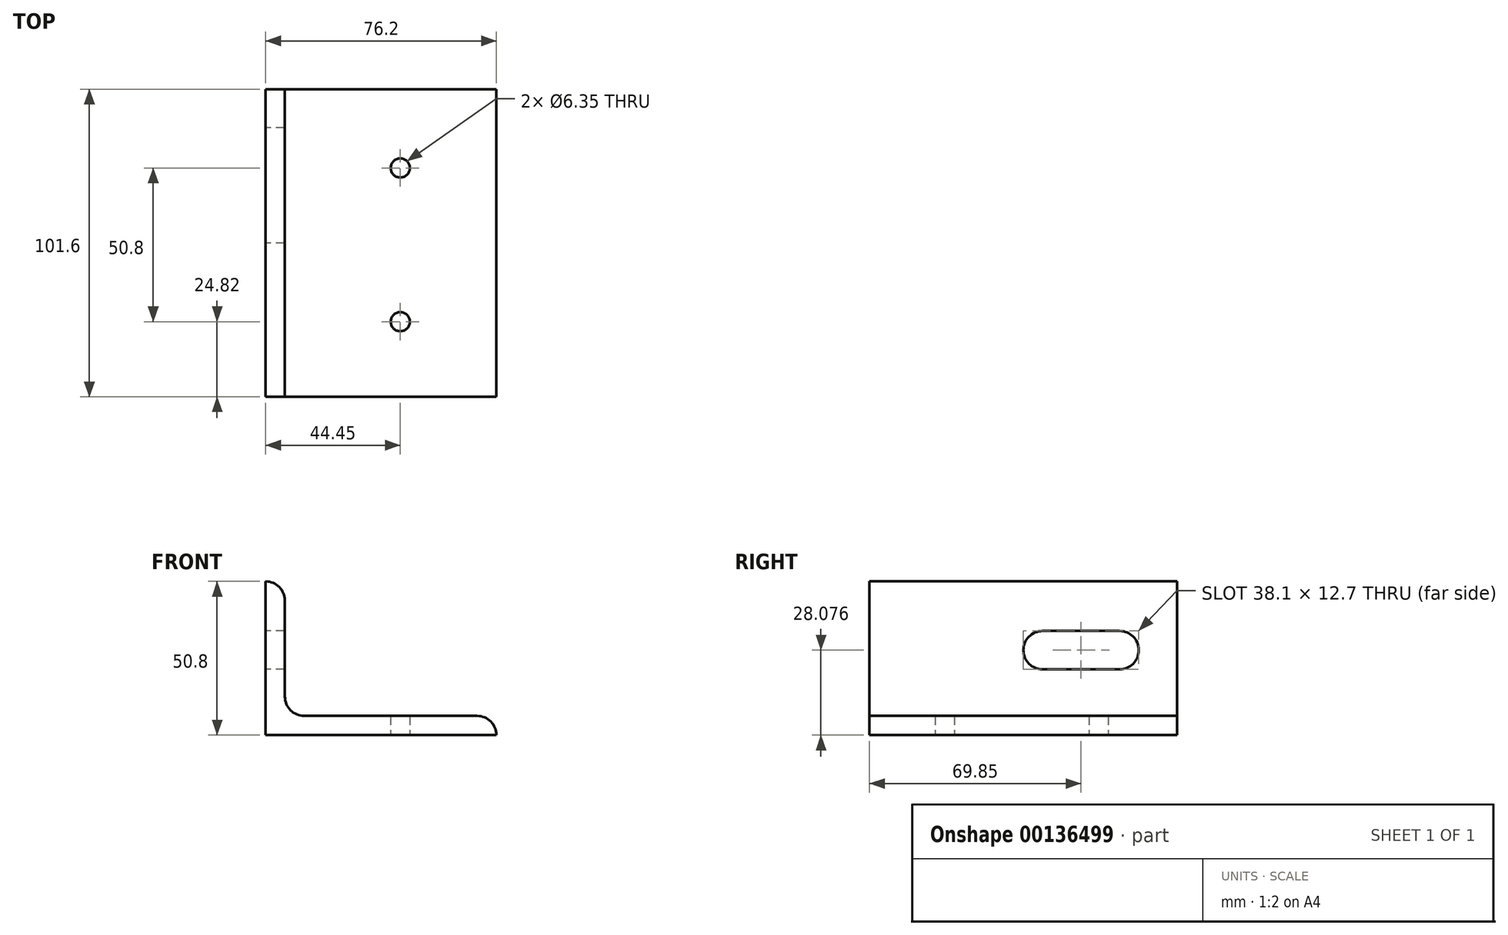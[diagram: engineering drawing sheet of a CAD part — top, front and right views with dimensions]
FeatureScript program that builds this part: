
annotation { "Feature Type Name" : "Feature", "Feature Type Description" : "" }
export const myFeature = defineFeature(function(context is Context, id is Id, definition is map)
    precondition{}
    {
        {
            var Q0;
            Q0=qCreatedBy(makeId("Front.planeOp"),FACE);
            var sketch = newSketch(context, id + "F0", { "sketchPlane" : qUnion([Q0])});
            skLineSegment(sketch, "E0", {"start": v(0, 50.8) * mm, "end": v(0, 0) * mm});
            skLineSegment(sketch, "E1", {"start": v(0, 0) * mm, "end": v(76.2, 0) * mm});
            skArc(sketch, "E2", {"start": v(6.35, 44.45) * mm, "mid": v(4.5, 48.94) * mm, "end": v(0, 50.8) * mm});
            skLineSegment(sketch, "E3", {"start": v(6.35, 44.45) * mm, "end": v(6.35, 6.35) * mm});
            skLineSegment(sketch, "E4", {"start": v(6.35, 6.35) * mm, "end": v(69.85, 6.35) * mm});
            skArc(sketch, "E5", {"start": v(76.2, 0) * mm, "mid": v(74.34, 4.5) * mm, "end": v(69.85, 6.35) * mm});
            skSolve(sketch);
        }
        {
            var Q0;
            Q0=makeQuery(id+"F0.imprint","IMPRINT",FACE,{"disambiguationData":[TD([[makeQuery(id+"F0.imprint","IMPRINT",EDGE,{"derivedFrom":sQuery(id+"F0.wireOp",EDGE,"E0")}),1.0]])]});
            extrude(context, id + "F1", {"entities" : qUnion([Q0]), "endBound" : BoundingType.SYMMETRIC, "depth" : 101.6 * mm});
        }
        {
            var Q0;
            Q0=makeQuery(id+"F1.opExtrude","SWEPT_EDGE",EDGE,{"disambiguationData":[OSD([sQuery(id+"F0.wireOp",EDGE,"E3"),sQuery(id+"F0.wireOp",EDGE,"E4")])]});
            fillet(context, id + "F2", {"entities" : qUnion([Q0]), "radius" : 6.35 * mm, "tangentPropagation" : true, "allowEdgeOverflow" : false});
        }
        {
            var Q0;
            Q0=makeQuery(id+"F1.opExtrude","SWEPT_FACE",FACE,{"disambiguationData":[OSD([sQuery(id+"F0.wireOp",EDGE,"E1")])]});
            var sketch = newSketch(context, id + "F3", { "sketchPlane" : qUnion([Q0])});
            skPoint(sketch, "E6", {"position": v(44.45, 25.98) * mm});
            skPoint(sketch, "E7", {"position": v(44.45, -24.82) * mm});
            skSolve(sketch);
        }
        {
            var Q0;
            Q0=sQuery(id+"F3.wireOp",VERTEX,"E6");
            var Q1;
            Q1=sQuery(id+"F3.wireOp",VERTEX,"E7");
            var Q2;
            Q2=makeQuery(id+"F1.opExtrude","SWEPT_BODY",BODY,{"disambiguationData":[OSD([sQuery(id+"F0.wireOp",EDGE,"E0"),sQuery(id+"F0.wireOp",EDGE,"E1"),sQuery(id+"F0.wireOp",EDGE,"E2"),sQuery(id+"F0.wireOp",EDGE,"E3"),sQuery(id+"F0.wireOp",EDGE,"E4"),sQuery(id+"F0.wireOp",EDGE,"E5")])]});
            hole(context, id + "F4", {"style" : HoleStyle.SIMPLE, "endStyle" : HoleEndStyle.THROUGH, "holeDiameter" : 6.35 * mm, "locations" : qUnion([Q0, Q1]), "scope" : qUnion([Q2]), "isTappedThrough" : true});
        }
        {
            var Q0;
            Q0=makeQuery(id+"F1.opExtrude","SWEPT_FACE",FACE,{"disambiguationData":[OSD([sQuery(id+"F0.wireOp",EDGE,"E0")])]});
            var sketch = newSketch(context, id + "F5", { "sketchPlane" : qUnion([Q0])});
            skArc(sketch, "E8", {"start": v(-31.75, 34.43) * mm, "mid": v(-38.1, 28.08) * mm, "end": v(-31.75, 21.73) * mm});
            skArc(sketch, "E9", {"start": v(-6.35, 21.73) * mm, "mid": v(0, 28.08) * mm, "end": v(-6.35, 34.43) * mm});
            skLineSegment(sketch, "E10", {"start": v(-31.75, 34.43) * mm, "end": v(-6.35, 34.43) * mm});
            skLineSegment(sketch, "E11", {"start": v(-31.75, 21.73) * mm, "end": v(-6.35, 21.73) * mm});
            skSolve(sketch);
        }
        {
            var Q0;
            Q0=makeQuery(id+"F5.imprint","IMPRINT",FACE,{"disambiguationData":[TD([[makeQuery(id+"F5.imprint","IMPRINT",EDGE,{"derivedFrom":sQuery(id+"F5.wireOp",EDGE,"E8")}),1.0]])]});
            extrude(context, id + "F6", {"entities" : qUnion([Q0]), "operationType" : NewBodyOperationType.REMOVE, "endBound" : BoundingType.THROUGH_ALL, "oppositeDirection" : true, "depth" : 25.4 * mm});
        }
    });
